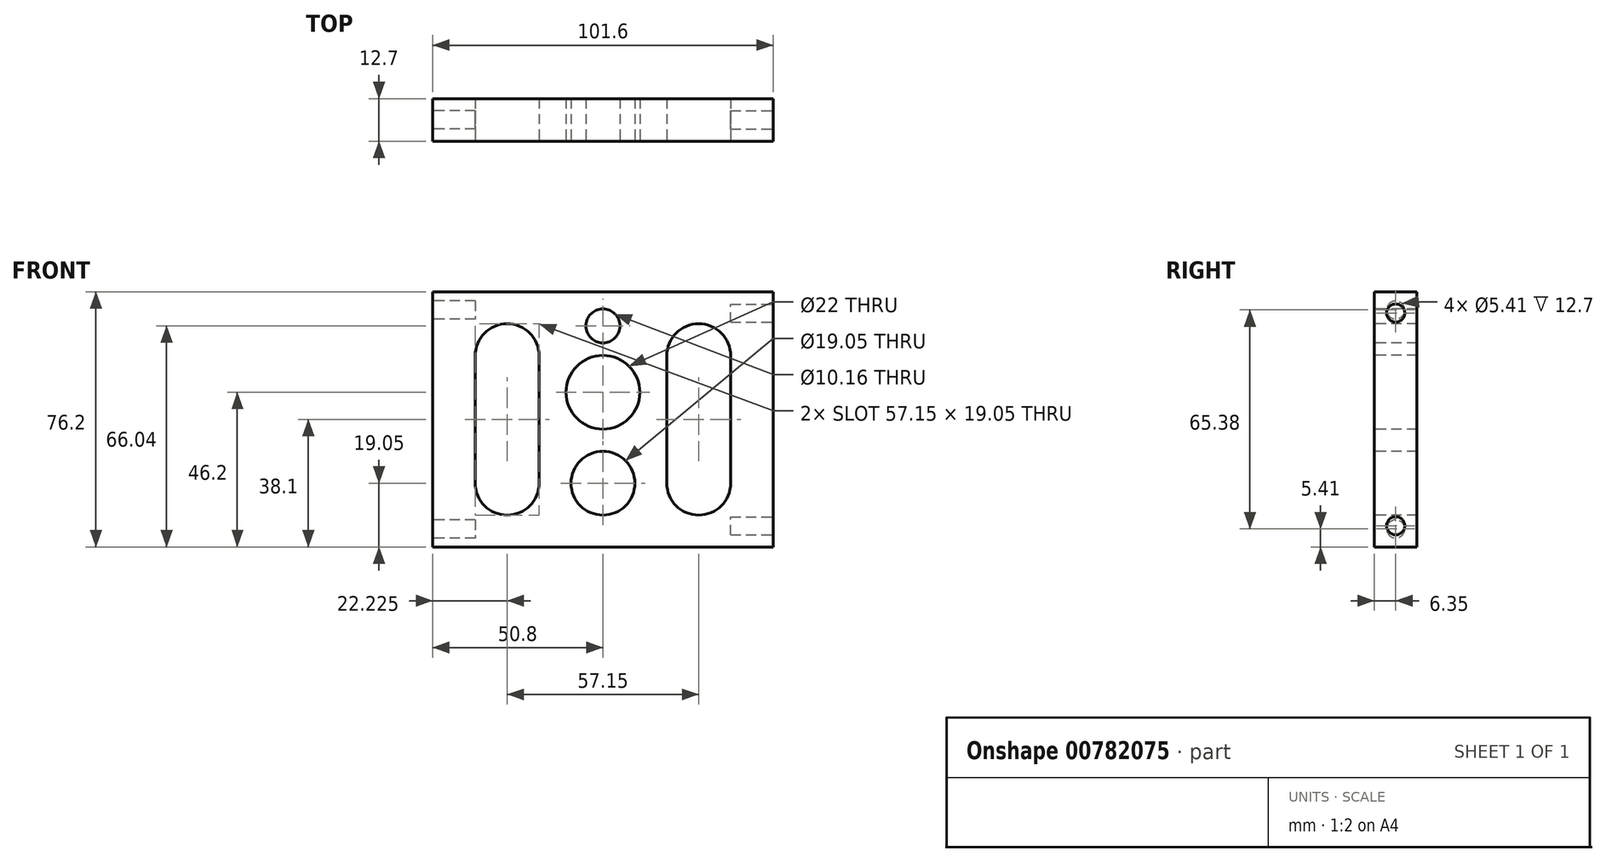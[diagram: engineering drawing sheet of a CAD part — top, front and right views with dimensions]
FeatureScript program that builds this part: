
annotation { "Feature Type Name" : "Feature", "Feature Type Description" : "" }
export const myFeature = defineFeature(function(context is Context, id is Id, definition is map)
    precondition{}
    {
        {
            var Q0;
            Q0=qCreatedBy(makeId("Front.planeOp"),FACE);
            var sketch = newSketch(context, id + "F0", { "sketchPlane" : qUnion([Q0])});
            skLineSegment(sketch, "E0.bottom", {"start": v(0, 0) * mm, "end": v(101.6, 0) * mm});
            skLineSegment(sketch, "E0.top", {"start": v(0, 76.2) * mm, "end": v(101.6, 76.2) * mm});
            skLineSegment(sketch, "E0.left", {"start": v(0, 0) * mm, "end": v(0, 76.2) * mm});
            skLineSegment(sketch, "E0.right", {"start": v(101.6, 0) * mm, "end": v(101.6, 76.2) * mm});
            skSolve(sketch);
        }
        {
            var Q0;
            Q0 = qSketchRegion(id + "F0", true);
            extrude(context, id + "F1", {"entities" : qUnion([Q0]), "depth" : 12.7 * mm, "offsetDistance" : 25.4 * mm});
        }
        {
            var Q0;
            Q0=makeQuery(id+"F1.opExtrude","CAP_FACE",FACE,{"disambiguationData":[OSD([sQuery(id+"F0.wireOp",EDGE,"E0.bottom"),sQuery(id+"F0.wireOp",EDGE,"E0.top"),sQuery(id+"F0.wireOp",EDGE,"E0.left"),sQuery(id+"F0.wireOp",EDGE,"E0.right")])],"isStart":false});
            var sketch = newSketch(context, id + "F2", { "sketchPlane" : qUnion([Q0])});
            skLineSegment(sketch, "E1", {"start": v(50.8, 76.2) * mm, "end": v(50.8, 0) * mm, "construction": true});
            skCircle(sketch, "E2", {"center": v(50.8, 46.2) * mm, "radius": 11 * mm});
            skSolve(sketch);
        }
        {
            var Q0;
            Q0 = qSketchRegion(id + "F2", true);
            extrude(context, id + "F3", {"entities" : qUnion([Q0]), "operationType" : NewBodyOperationType.REMOVE, "oppositeDirection" : true, "depth" : 25.4 * mm, "offsetDistance" : 25.4 * mm});
        }
        {
            var Q0;
            Q0=makeQuery(id+"F1.opExtrude","CAP_FACE",FACE,{"disambiguationData":[OSD([sQuery(id+"F0.wireOp",EDGE,"E0.bottom"),sQuery(id+"F0.wireOp",EDGE,"E0.top"),sQuery(id+"F0.wireOp",EDGE,"E0.left"),sQuery(id+"F0.wireOp",EDGE,"E0.right")])],"isStart":false});
            var sketch = newSketch(context, id + "F4", { "sketchPlane" : qUnion([Q0])});
            skLineSegment(sketch, "E3", {"start": v(50.8, 76.2) * mm, "end": v(50.8, 0) * mm, "construction": true});
            skCircle(sketch, "E4", {"center": v(50.8, 19.05) * mm, "radius": 9.53 * mm});
            skLineSegment(sketch, "E5", {"start": v(12.7, 57.15) * mm, "end": v(12.7, 19.05) * mm});
            skLineSegment(sketch, "E6", {"start": v(31.75, 57.15) * mm, "end": v(31.75, 19.05) * mm});
            skArc(sketch, "E7", {"start": v(12.7, 57.15) * mm, "mid": v(22.23, 66.68) * mm, "end": v(31.75, 57.15) * mm});
            skArc(sketch, "E8", {"start": v(31.75, 19.05) * mm, "mid": v(22.23, 9.53) * mm, "end": v(12.7, 19.05) * mm});
            skLineSegment(sketch, "E9", {"start": v(50.8, 38.1) * mm, "end": v(0, 38.1) * mm});
            skLineSegment(sketch, "E10", {"start": v(12.7, 38.1) * mm, "end": v(31.75, 38.1) * mm, "construction": true});
            skLineSegment(sketch, "E11.MirrorCS", {"start": v(69.85, 57.15) * mm, "end": v(69.85, 19.05) * mm});
            skArc(sketch, "E12.MirrorCS", {"start": v(88.9, 57.15) * mm, "mid": v(79.37, 66.68) * mm, "end": v(69.85, 57.15) * mm});
            skLineSegment(sketch, "E13.MirrorCS", {"start": v(88.9, 57.15) * mm, "end": v(88.9, 19.05) * mm});
            skArc(sketch, "E14.MirrorCS", {"start": v(69.85, 19.05) * mm, "mid": v(79.37, 9.52) * mm, "end": v(88.9, 19.05) * mm});
            skCircle(sketch, "E15", {"center": v(50.8, 66.04) * mm, "radius": 5.08 * mm});
            skSolve(sketch);
        }
        {
            var Q0;
            Q0 = qSketchRegion(id + "F4", true);
            extrude(context, id + "F5", {"entities" : qUnion([Q0]), "operationType" : NewBodyOperationType.REMOVE, "oppositeDirection" : true, "depth" : 25.4 * mm, "offsetDistance" : 25.4 * mm});
        }
        {
            var Q0;
            Q0=makeQuery(id+"F1.opExtrude","SWEPT_FACE",FACE,{"disambiguationData":[OSD([sQuery(id+"F0.wireOp",EDGE,"E0.right")])]});
            var sketch = newSketch(context, id + "F6", { "sketchPlane" : qUnion([Q0])});
            skLineSegment(sketch, "E16", {"start": v(-6.35, 76.2) * mm, "end": v(-6.35, 0) * mm, "construction": true});
            skCircle(sketch, "E17", {"center": v(-6.35, 69.85) * mm, "radius": 2.7 * mm});
            skCircle(sketch, "E18", {"center": v(-6.35, 6.35) * mm, "radius": 2.7 * mm});
            skSolve(sketch);
        }
        {
            var Q0;
            Q0 = qSketchRegion(id + "F6", true);
            extrude(context, id + "F7", {"entities" : qUnion([Q0]), "operationType" : NewBodyOperationType.REMOVE, "oppositeDirection" : true, "depth" : 12.7 * mm, "offsetDistance" : 25.4 * mm});
        }
        {
            var Q0;
            Q0=makeQuery(id+"F1.opExtrude","SWEPT_FACE",FACE,{"disambiguationData":[OSD([sQuery(id+"F0.wireOp",EDGE,"E0.left")])]});
            var sketch = newSketch(context, id + "F8", { "sketchPlane" : qUnion([Q0])});
            skLineSegment(sketch, "E19", {"start": v(6.35, 76.2) * mm, "end": v(6.35, 0) * mm, "construction": true});
            skCircle(sketch, "E20", {"center": v(6.35, 70.79) * mm, "radius": 2.7 * mm});
            skCircle(sketch, "E21", {"center": v(6.35, 5.41) * mm, "radius": 2.7 * mm});
            skSolve(sketch);
        }
        {
            var Q0;
            Q0 = qSketchRegion(id + "F8", true);
            extrude(context, id + "F9", {"entities" : qUnion([Q0]), "operationType" : NewBodyOperationType.REMOVE, "oppositeDirection" : true, "depth" : 12.7 * mm, "offsetDistance" : 25.4 * mm});
        }
    });
